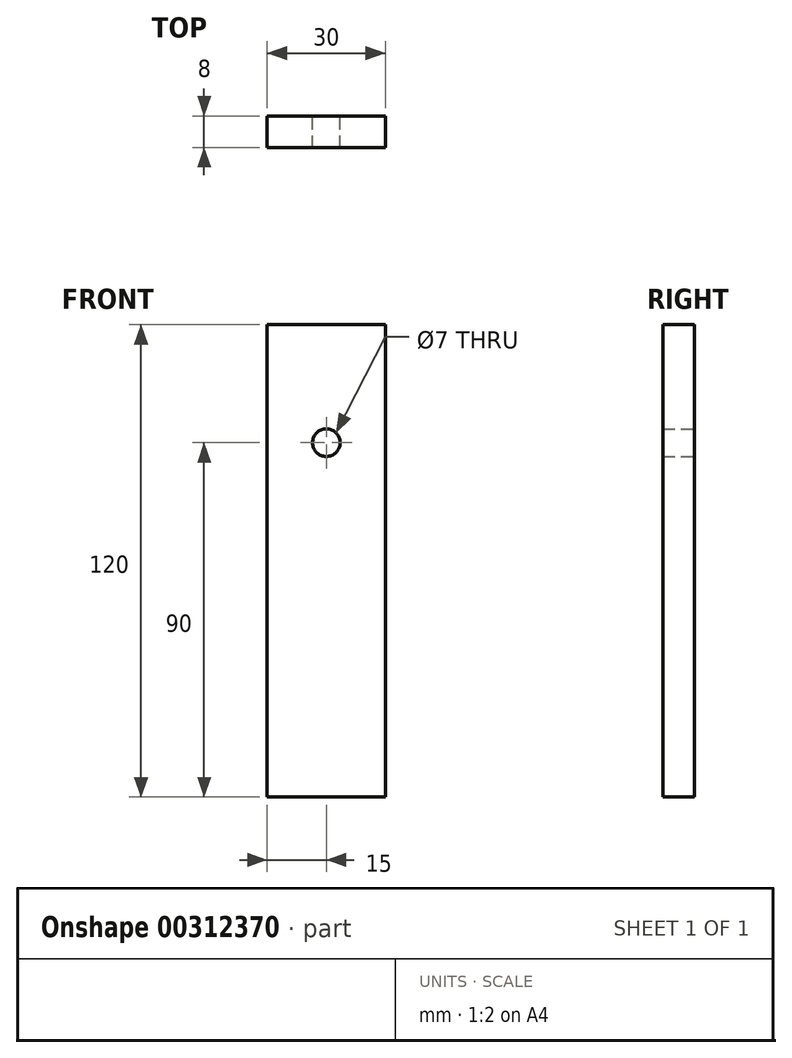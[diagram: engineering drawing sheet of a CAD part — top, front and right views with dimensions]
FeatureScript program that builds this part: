
annotation { "Feature Type Name" : "Feature", "Feature Type Description" : "" }
export const myFeature = defineFeature(function(context is Context, id is Id, definition is map)
    precondition{}
    {
        {
            var Q0;
            Q0=qCreatedBy(makeId("Front.planeOp"),FACE);
            var sketch = newSketch(context, id + "F0", { "sketchPlane" : qUnion([Q0])});
            skLineSegment(sketch, "E0.bottom", {"start": v(15, 60) * mm, "end": v(-15, 60) * mm});
            skLineSegment(sketch, "E0.top", {"start": v(15, -60) * mm, "end": v(-15, -60) * mm});
            skLineSegment(sketch, "E0.left", {"start": v(15, 60) * mm, "end": v(15, -60) * mm});
            skLineSegment(sketch, "E0.right", {"start": v(-15, 60) * mm, "end": v(-15, -60) * mm});
            skPoint(sketch, "E0.middle", {"position": v(0, 0) * mm});
            skCircle(sketch, "E1", {"center": v(0, 30) * mm, "radius": 3.5 * mm});
            skSolve(sketch);
        }
        {
            var Q0;
            Q0=makeQuery(id+"F0.imprint","IMPRINT",FACE,{"disambiguationData":[TD([[makeQuery(id+"F0.imprint","IMPRINT",EDGE,{"derivedFrom":sQuery(id+"F0.wireOp",EDGE,"E0.bottom")}),1.0]])]});
            extrude(context, id + "F1", {"entities" : qUnion([Q0]), "depth" : 8 * mm});
        }
    });
